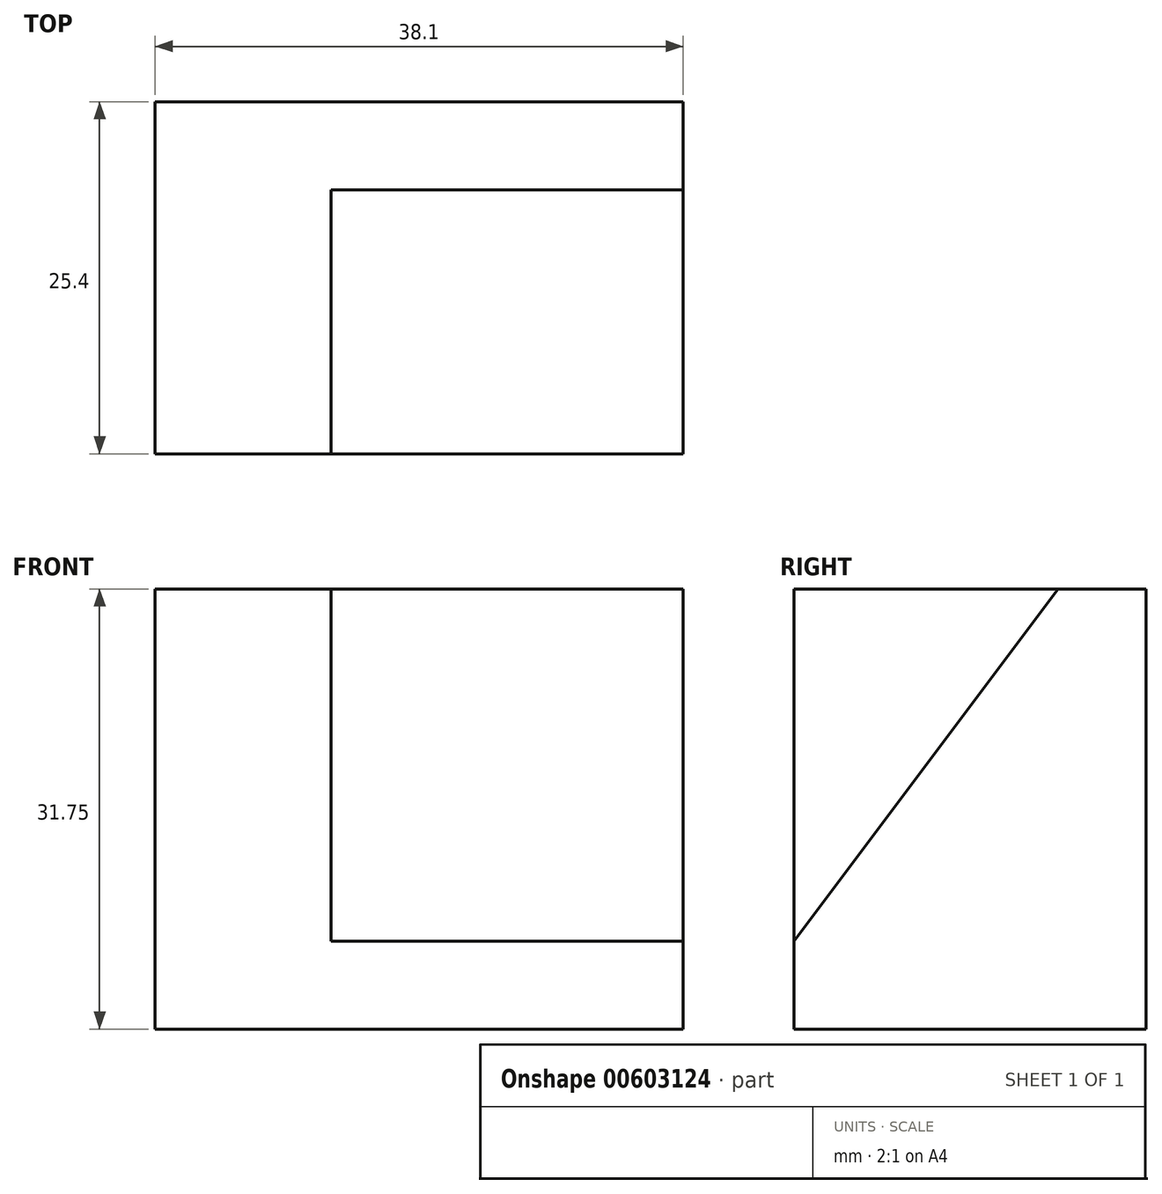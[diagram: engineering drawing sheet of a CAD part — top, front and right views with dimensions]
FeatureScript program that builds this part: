
annotation { "Feature Type Name" : "Feature", "Feature Type Description" : "" }
export const myFeature = defineFeature(function(context is Context, id is Id, definition is map)
    precondition{}
    {
        {
            var Q0;
            Q0=qCreatedBy(makeId("Front.planeOp"),FACE);
            var sketch = newSketch(context, id + "F0", { "sketchPlane" : qUnion([Q0])});
            skLineSegment(sketch, "E0", {"start": v(0, 0) * mm, "end": v(0, 31.75) * mm});
            skLineSegment(sketch, "E1", {"start": v(0, 31.75) * mm, "end": v(38.1, 31.75) * mm});
            skLineSegment(sketch, "E2", {"start": v(38.1, 31.75) * mm, "end": v(38.1, 0) * mm});
            skLineSegment(sketch, "E3", {"start": v(38.1, 0) * mm, "end": v(0, 0) * mm});
            skSolve(sketch);
        }
        {
            var Q0;
            Q0 = qSketchRegion(id + "F0", true);
            extrude(context, id + "F1", {"entities" : qUnion([Q0]), "depth" : 25.4 * mm, "offsetDistance" : 25.4 * mm});
        }
        {
            var Q0;
            Q0=makeQuery(id+"F1.opExtrude","SWEPT_FACE",FACE,{"disambiguationData":[OSD([sQuery(id+"F0.wireOp",EDGE,"E2")])]});
            var sketch = newSketch(context, id + "F2", { "sketchPlane" : qUnion([Q0])});
            skLineSegment(sketch, "E4", {"start": v(0, 31.75) * mm, "end": v(-6.35, 31.75) * mm});
            skLineSegment(sketch, "E5", {"start": v(0, 31.75) * mm, "end": v(0, 0) * mm});
            skLineSegment(sketch, "E6", {"start": v(0, 0) * mm, "end": v(-25.4, 0) * mm});
            skLineSegment(sketch, "E7", {"start": v(-25.4, 0) * mm, "end": v(-25.4, 6.35) * mm});
            skLineSegment(sketch, "E8", {"start": v(-25.4, 6.35) * mm, "end": v(-6.35, 31.75) * mm});
            skLineSegment(sketch, "E9", {"start": v(-6.35, 31.75) * mm, "end": v(-25.4, 31.75) * mm});
            skLineSegment(sketch, "E10", {"start": v(-25.4, 31.75) * mm, "end": v(-25.4, 6.35) * mm});
            skSolve(sketch);
        }
        {
            var Q0;
            Q0=makeQuery(id+"F2.imprint","IMPRINT",FACE,{"disambiguationData":[TD([[makeQuery(id+"F2.imprint","IMPRINT",EDGE,{"derivedFrom":sQuery(id+"F2.wireOp",EDGE,"E9")}),-1.0]])]});
            extrude(context, id + "F3", {"entities" : qUnion([Q0]), "operationType" : NewBodyOperationType.REMOVE, "oppositeDirection" : true, "depth" : 25.4 * mm, "offsetDistance" : 25.4 * mm});
        }
    });
